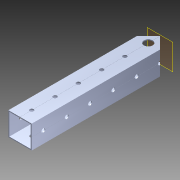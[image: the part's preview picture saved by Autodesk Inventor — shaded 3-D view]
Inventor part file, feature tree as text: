
AUTODESK INVENTOR PART (.ipt)
format: ipt  version: 2014 SP1 (Build 180222100, 222)  size: 1,208,832 bytes
history: native  units: in
note: dims shown in document units (in); Inventor stores cm internally (conversion verified against a paired STEP export)
features: extrude x3, sketch x2, pattern_circular x1, other x1, plane x1, imported_body x1
ambient origin geometry x8: Origin, YZ Plane, XZ Plane, XY Plane, X Axis, Y Axis, Z Axis, Center Point
bodies: Body1 (feature_tree)
feature tree (9):
  pattern_circular  "CirPattern2"
  other  "217-3426-STEP1"
  plane  "Work Plane1"
  extrude  "Extrusion1"  Depth=393.7008in TaperAngle=0.0deg
  extrude  "Extrusion3"  Depth=1.0in TaperAngle=0.0deg
  extrude  "Extrusion4"  TaperAngle=45.0deg  [1 undecoded]
  imported_body  "Base1"
  sketch  "Sketch1"  dims[d0=-6.0in d1=393.7008in d2=0.0in]
  sketch  "Sketch4"  dims[d8=0.5in d9=1.0in d10=0.0in d12=45.0deg d15=1.0in d16=0.375in d17=39.3701in d18=0.0in]
note: 1 required parameter value undecoded (feature->parameter linkage not recoverable at this tier; creation-order binding heuristic only, values carry confidence <= 0.55)
